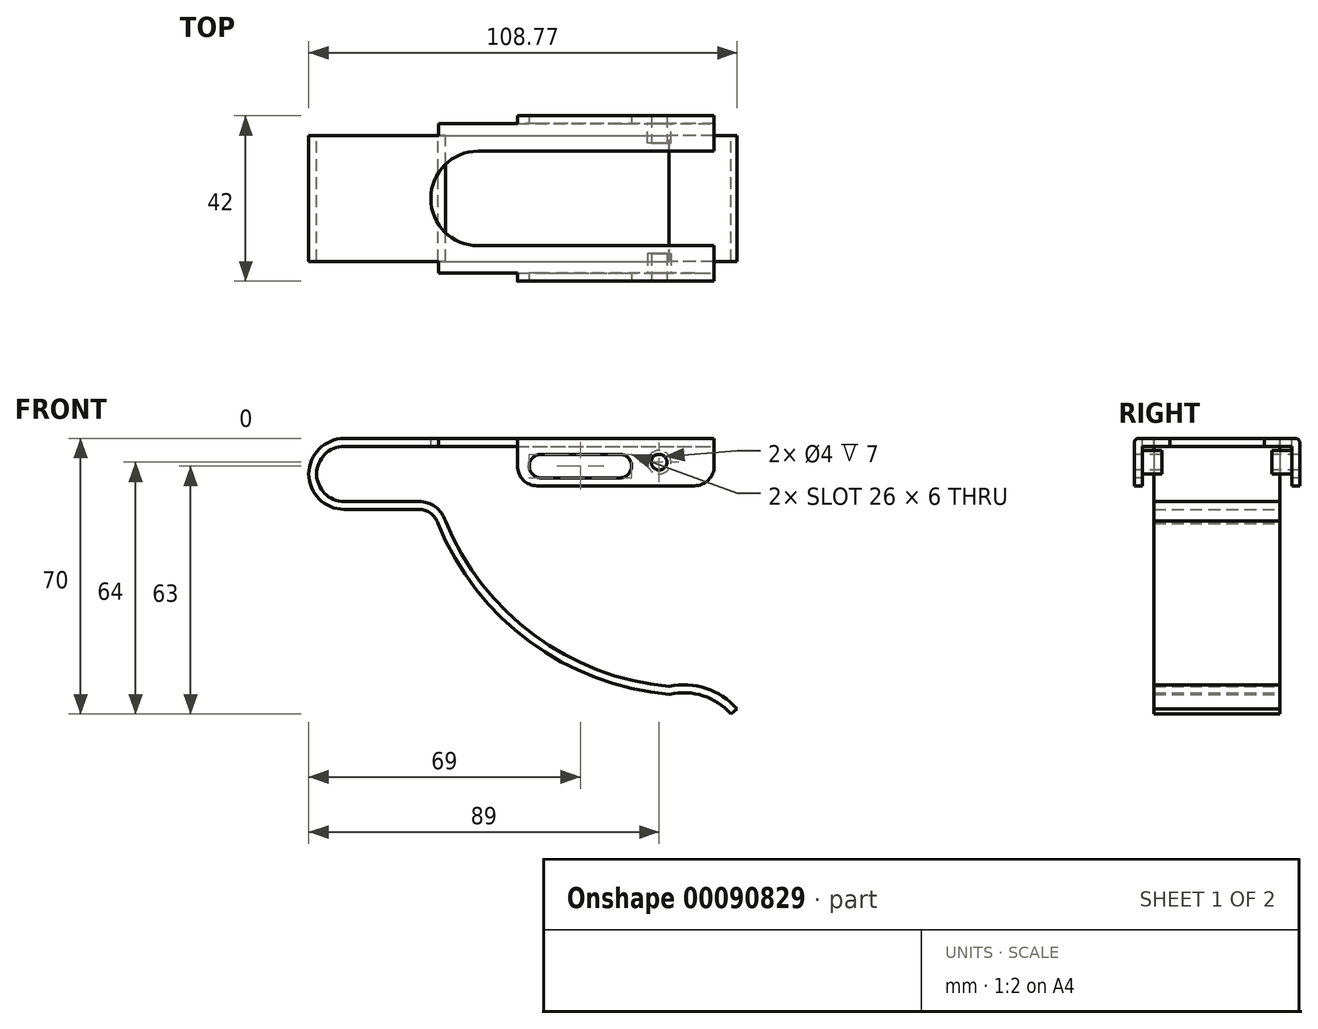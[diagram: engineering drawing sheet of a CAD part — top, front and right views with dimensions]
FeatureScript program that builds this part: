
annotation { "Feature Type Name" : "Feature", "Feature Type Description" : "" }
export const myFeature = defineFeature(function(context is Context, id is Id, definition is map)
    precondition{}
    {
        {
            var Q0;
            Q0=qCreatedBy(makeId("Front.planeOp"),FACE);
            var sketch = newSketch(context, id + "F0", { "sketchPlane" : qUnion([Q0])});
            skArc(sketch, "E0", {"start": v(0, 9) * mm, "mid": v(-9, 0) * mm, "end": v(0, -9) * mm});
            skLineSegment(sketch, "E1", {"start": v(0, 41.41) * mm, "end": v(0, 0) * mm, "construction": true});
            skLineSegment(sketch, "E2", {"start": v(0, 0) * mm, "end": v(0, -47.46) * mm, "construction": true});
            skLineSegment(sketch, "E3", {"start": v(0, 9) * mm, "end": v(94, 9) * mm});
            skLineSegment(sketch, "E4", {"start": v(0, -9) * mm, "end": v(19, -9) * mm});
            skPoint(sketch, "E5.visualSharp", {"position": v(22.93, -9) * mm});
            skArc(sketch, "E5.filletArc", {"start": v(23.8, -12.6) * mm, "mid": v(22, -10) * mm, "end": v(19, -9) * mm});
            skArc(sketch, "E6", {"start": v(23.8, -12.6) * mm, "mid": v(47.11, -42.6) * mm, "end": v(82.67, -56) * mm});
            skArc(sketch, "E7", {"start": v(98.27, -61) * mm, "mid": v(91.16, -56.35) * mm, "end": v(82.67, -56) * mm});
            skLineSegment(sketch, "E8.0", {"start": v(0, 7) * mm, "end": v(94, 7) * mm});
            skArc(sketch, "E8.1", {"start": v(0, 7) * mm, "mid": v(-7, 0) * mm, "end": v(0, -7) * mm});
            skArc(sketch, "E8.2", {"start": v(99.77, -59.68) * mm, "mid": v(91.92, -54.5) * mm, "end": v(82.54, -53.98) * mm});
            skArc(sketch, "E8.3", {"start": v(25.69, -11.92) * mm, "mid": v(48.21, -40.92) * mm, "end": v(82.54, -53.98) * mm});
            skArc(sketch, "E8.4", {"start": v(25.69, -11.92) * mm, "mid": v(23.15, -8.36) * mm, "end": v(19, -7) * mm});
            skLineSegment(sketch, "E8.5", {"start": v(0, -7) * mm, "end": v(19, -7) * mm});
            skLineSegment(sketch, "E9", {"start": v(99.77, -59.68) * mm, "end": v(98.27, -61) * mm});
            skLineSegment(sketch, "E10", {"start": v(94, 7) * mm, "end": v(94, 9) * mm});
            skSolve(sketch);
        }
        {
            var Q0;
            Q0=makeQuery(id+"F0.imprint","IMPRINT",FACE,{"disambiguationData":[TD([[makeQuery(id+"F0.imprint","IMPRINT",EDGE,{"derivedFrom":sQuery(id+"F0.wireOp",EDGE,"E0")}),1.0]])]});
            extrude(context, id + "F1", {"entities" : qUnion([Q0]), "depth" : 16 * mm});
        }
        {
            var Q0;
            Q0=makeQuery(id+"F1.opExtrude","SWEPT_FACE",FACE,{"disambiguationData":[OSD([sQuery(id+"F0.wireOp",EDGE,"E3")])]});
            var sketch = newSketch(context, id + "F2", { "sketchPlane" : qUnion([Q0])});
            skLineSegment(sketch, "E11.bottom", {"start": v(24, -16) * mm, "end": v(94, -16) * mm});
            skLineSegment(sketch, "E11.top", {"start": v(24, -19) * mm, "end": v(94, -19) * mm});
            skLineSegment(sketch, "E11.left", {"start": v(24, -16) * mm, "end": v(24, -19) * mm});
            skLineSegment(sketch, "E11.right", {"start": v(94, -16) * mm, "end": v(94, -19) * mm});
            skSolve(sketch);
        }
        {
            var Q0;
            Q0 = qSketchRegion(id + "F2", true);
            extrude(context, id + "F3", {"entities" : qUnion([Q0]), "operationType" : NewBodyOperationType.ADD, "oppositeDirection" : true, "depth" : 2 * mm});
        }
        {
            var Q0;
            Q0=makeQuery(id+"F3.opExtrude","SWEPT_FACE",FACE,{"disambiguationData":[OSD([sQuery(id+"F2.wireOp",EDGE,"E11.top")])]});
            var sketch = newSketch(context, id + "F4", { "sketchPlane" : qUnion([Q0])});
            skLineSegment(sketch, "E12.bottom", {"start": v(94, 9) * mm, "end": v(44, 9) * mm});
            skLineSegment(sketch, "E12.top", {"start": v(94, -3) * mm, "end": v(44, -3) * mm});
            skLineSegment(sketch, "E12.left", {"start": v(94, 9) * mm, "end": v(94, -3) * mm});
            skLineSegment(sketch, "E12.right", {"start": v(44, 9) * mm, "end": v(44, -3) * mm});
            skSolve(sketch);
        }
        {
            var Q0;
            Q0 = qSketchRegion(id + "F4", true);
            extrude(context, id + "F5", {"entities" : qUnion([Q0]), "operationType" : NewBodyOperationType.ADD, "depth" : 2 * mm});
        }
        {
            var Q0;
            Q0=makeQuery(id+"F5.opExtrude","CAP_EDGE",EDGE,{"disambiguationData":[OSD([sQuery(id+"F4.wireOp",EDGE,"E12.bottom")])],"isStart":false});
            fillet(context, id + "F6", {"entities" : qUnion([Q0]), "radius" : 1 * mm, "allowEdgeOverflow" : false});
        }
        {
            var Q0;
            Q0=makeQuery(id+"F1.opExtrude","SWEPT_BODY",BODY,{"disambiguationData":[OSD([sQuery(id+"F0.wireOp",EDGE,"E0"),sQuery(id+"F0.wireOp",EDGE,"E3"),sQuery(id+"F0.wireOp",EDGE,"E4"),sQuery(id+"F0.wireOp",EDGE,"E5.filletArc"),sQuery(id+"F0.wireOp",EDGE,"E6"),sQuery(id+"F0.wireOp",EDGE,"E7"),sQuery(id+"F0.wireOp",EDGE,"E8.0"),sQuery(id+"F0.wireOp",EDGE,"E8.1"),sQuery(id+"F0.wireOp",EDGE,"E8.2"),sQuery(id+"F0.wireOp",EDGE,"E8.3"),sQuery(id+"F0.wireOp",EDGE,"E8.4"),sQuery(id+"F0.wireOp",EDGE,"E8.5"),sQuery(id+"F0.wireOp",EDGE,"E9"),sQuery(id+"F0.wireOp",EDGE,"E10")])]});
            var Q1;
            Q1=qCreatedBy(makeId("Front.planeOp"),FACE);
            mirror(context, id + "F7", {"operationType" : NewBodyOperationType.ADD, "entities" : qUnion([Q0]), "mirrorPlane" : qUnion([Q1])});
        }
        {
            var Q0;
            {var subQ0=makeQuery(id+"F5.boolean.opBoolean","MERGE",FACE,{"derivedFrom":[makeQuery(id+"F3.boolean.opBoolean","MERGE",FACE,{"derivedFrom":[makeQuery(id+"F1.opExtrude","SWEPT_FACE",FACE,{"disambiguationData":[OSD([sQuery(id+"F0.wireOp",EDGE,"E3")])]}),makeQuery(id+"F3.opExtrude","CAP_FACE",FACE,{"disambiguationData":[OSD([sQuery(id+"F2.wireOp",EDGE,"E11.bottom"),sQuery(id+"F2.wireOp",EDGE,"E11.top"),sQuery(id+"F2.wireOp",EDGE,"E11.left"),sQuery(id+"F2.wireOp",EDGE,"E11.right")])],"isStart":true})]}),makeQuery(id+"F5.opExtrude","SWEPT_FACE",FACE,{"disambiguationData":[OSD([sQuery(id+"F4.wireOp",EDGE,"E12.bottom")])]})]});Q0=makeQuery(id+"F7.boolean.opBoolean","MERGE",FACE,{"derivedFrom":[subQ0,makeQuery(id+"F7.opPattern","COPY",FACE,{"derivedFrom":subQ0,"instanceName":"1"})]});}
            var sketch = newSketch(context, id + "F8", { "sketchPlane" : qUnion([Q0])});
            skArc(sketch, "E13", {"start": v(34, 12) * mm, "mid": v(22, 0) * mm, "end": v(34, -12) * mm});
            skLineSegment(sketch, "E14", {"start": v(34, -12) * mm, "end": v(94, -12) * mm});
            skLineSegment(sketch, "E15", {"start": v(34, 12) * mm, "end": v(94, 12) * mm});
            skSolve(sketch);
        }
        {
            var Q0;
            Q0 = qSketchRegion(id + "F8", true);
            var Q1;
            Q1=makeQuery(id+"F8.imprint","IMPRINT",FACE,{"disambiguationData":[TD([[makeQuery(id+"F8.imprint","IMPRINT",EDGE,{"derivedFrom":sQuery(id+"F8.wireOp",EDGE,"E13")}),1.0]])]});
            extrude(context, id + "F9", {"entities" : qUnion([Q0, Q1]), "operationType" : NewBodyOperationType.REMOVE, "oppositeDirection" : true, "depth" : 9.3 * mm});
        }
        {
            var Q0;
            Q0=makeQuery(id+"F5.opExtrude","CAP_FACE",FACE,{"disambiguationData":[OSD([sQuery(id+"F4.wireOp",EDGE,"E12.bottom"),sQuery(id+"F4.wireOp",EDGE,"E12.top"),sQuery(id+"F4.wireOp",EDGE,"E12.left"),sQuery(id+"F4.wireOp",EDGE,"E12.right")])],"isStart":false});
            var sketch = newSketch(context, id + "F10", { "sketchPlane" : qUnion([Q0])});
            skLineSegment(sketch, "E16", {"start": v(50, 2) * mm, "end": v(70, 2) * mm});
            skArc(sketch, "E17.0.startCap", {"start": v(50, -1) * mm, "mid": v(47, 2) * mm, "end": v(50, 5) * mm});
            skArc(sketch, "E17.0.endCap", {"start": v(70, 5) * mm, "mid": v(73, 2) * mm, "end": v(70, -1) * mm});
            skLineSegment(sketch, "E17.0.left", {"start": v(50, 5) * mm, "end": v(70, 5) * mm});
            skLineSegment(sketch, "E17.0.right", {"start": v(50, -1) * mm, "end": v(70, -1) * mm});
            skSolve(sketch);
        }
        {
            var Q0;
            Q0 = qSketchRegion(id + "F10", true);
            extrude(context, id + "F11", {"entities" : qUnion([Q0]), "operationType" : NewBodyOperationType.REMOVE, "oppositeDirection" : true, "depth" : 109 * mm});
        }
        {
            var Q0;
            Q0=makeQuery(id+"F5.opExtrude","CAP_FACE",FACE,{"disambiguationData":[OSD([sQuery(id+"F4.wireOp",EDGE,"E12.bottom"),sQuery(id+"F4.wireOp",EDGE,"E12.top"),sQuery(id+"F4.wireOp",EDGE,"E12.left"),sQuery(id+"F4.wireOp",EDGE,"E12.right")])],"isStart":false});
            var sketch = newSketch(context, id + "F12", { "sketchPlane" : qUnion([Q0])});
            skPoint(sketch, "E18", {"position": v(80, 3) * mm});
            skSolve(sketch);
        }
        {
            var Q0;
            Q0=sQuery(id+"F12.wireOp",VERTEX,"E18");
            var Q1;
            Q1=makeQuery(id+"F1.opExtrude","SWEPT_BODY",BODY,{"disambiguationData":[OSD([sQuery(id+"F0.wireOp",EDGE,"E0"),sQuery(id+"F0.wireOp",EDGE,"E3"),sQuery(id+"F0.wireOp",EDGE,"E4"),sQuery(id+"F0.wireOp",EDGE,"E5.filletArc"),sQuery(id+"F0.wireOp",EDGE,"E6"),sQuery(id+"F0.wireOp",EDGE,"E7"),sQuery(id+"F0.wireOp",EDGE,"E8.0"),sQuery(id+"F0.wireOp",EDGE,"E8.1"),sQuery(id+"F0.wireOp",EDGE,"E8.2"),sQuery(id+"F0.wireOp",EDGE,"E8.3"),sQuery(id+"F0.wireOp",EDGE,"E8.4"),sQuery(id+"F0.wireOp",EDGE,"E8.5"),sQuery(id+"F0.wireOp",EDGE,"E9"),sQuery(id+"F0.wireOp",EDGE,"E10")])]});
            hole(context, id + "F13", {"style" : HoleStyle.SIMPLE, "endStyle" : HoleEndStyle.THROUGH, "holeDiameter" : 4 * mm, "locations" : qUnion([Q0]), "scope" : qUnion([Q1]), "isTappedThrough" : true});
        }
        {
            var Q0;
            Q0=makeQuery(id+"F5.opExtrude","CAP_FACE",FACE,{"disambiguationData":[OSD([sQuery(id+"F4.wireOp",EDGE,"E12.bottom"),sQuery(id+"F4.wireOp",EDGE,"E12.top"),sQuery(id+"F4.wireOp",EDGE,"E12.left"),sQuery(id+"F4.wireOp",EDGE,"E12.right")])],"isStart":true});
            var sketch = newSketch(context, id + "F14", { "sketchPlane" : qUnion([Q0])});
            skCircle(sketch, "E19.0", {"center": v(-80, 3) * mm, "radius": 2 * mm});
            skCircle(sketch, "E20.0", {"center": v(-80, 3) * mm, "radius": 3 * mm});
            skSolve(sketch);
        }
        {
            var Q0;
            Q0 = qSketchRegion(id + "F14", true);
            extrude(context, id + "F15", {"entities" : qUnion([Q0]), "operationType" : NewBodyOperationType.ADD, "depth" : 5 * mm});
        }
        {
            var Q0;
            Q0=makeQuery(id+"F7.opPattern","COPY",FACE,{"derivedFrom":makeQuery(id+"F5.opExtrude","CAP_FACE",FACE,{"disambiguationData":[OSD([sQuery(id+"F4.wireOp",EDGE,"E12.bottom"),sQuery(id+"F4.wireOp",EDGE,"E12.top"),sQuery(id+"F4.wireOp",EDGE,"E12.left"),sQuery(id+"F4.wireOp",EDGE,"E12.right")])],"isStart":true}),"instanceName":"1"});
            var sketch = newSketch(context, id + "F16", { "sketchPlane" : qUnion([Q0])});
            skCircle(sketch, "E21.0", {"center": v(80, 3) * mm, "radius": 2 * mm});
            skCircle(sketch, "E22.0", {"center": v(80, 3) * mm, "radius": 3 * mm});
            skSolve(sketch);
        }
        {
            var Q0;
            Q0 = qSketchRegion(id + "F16", true);
            extrude(context, id + "F17", {"entities" : qUnion([Q0]), "operationType" : NewBodyOperationType.ADD, "depth" : 5 * mm});
        }
        {
            var Q0;
            Q0=makeQuery(id+"F5.opExtrude","SWEPT_EDGE",EDGE,{"disambiguationData":[OSD([sQuery(id+"F4.wireOp",EDGE,"E12.top"),sQuery(id+"F4.wireOp",EDGE,"E12.left")])]});
            var Q1;
            Q1=makeQuery(id+"F7.opPattern","COPY",EDGE,{"derivedFrom":makeQuery(id+"F5.opExtrude","SWEPT_EDGE",EDGE,{"disambiguationData":[OSD([sQuery(id+"F4.wireOp",EDGE,"E12.top"),sQuery(id+"F4.wireOp",EDGE,"E12.left")])]}),"instanceName":"1"});
            var Q2;
            Q2=makeQuery(id+"F5.opExtrude","SWEPT_EDGE",EDGE,{"disambiguationData":[OSD([sQuery(id+"F4.wireOp",EDGE,"E12.top"),sQuery(id+"F4.wireOp",EDGE,"E12.right")])]});
            var Q3;
            Q3=makeQuery(id+"F7.opPattern","COPY",EDGE,{"derivedFrom":makeQuery(id+"F5.opExtrude","SWEPT_EDGE",EDGE,{"disambiguationData":[OSD([sQuery(id+"F4.wireOp",EDGE,"E12.top"),sQuery(id+"F4.wireOp",EDGE,"E12.right")])]}),"instanceName":"1"});
            fillet(context, id + "F18", {"entities" : qUnion([Q0, Q1, Q2, Q3]), "radius" : 5 * mm, "tangentPropagation" : true, "allowEdgeOverflow" : false});
        }
    });
